# Revit family: Grab_Bar-Ligature_Resistant-Whitehall_Manufacturing_BestCare-WHB-GB_Series
name_source: partatom
category: Specialty Equipment
units: mm (PartAtom-declared; Revit-internal decimal feet)

## family parameters
Cut with Voids When Loaded = No
Host = Face
OmniClass Number = 23.40.20.21.47
OmniClass Title = Bath Grab Bars
Part Type = Normal
Room Calculation Point = No
Round Connector Dimension = Use Diameter
Shared = Yes

## types (6) — shared parameters
ADA Compliant = Yes
Assembly Code = C1030200
Bar Depth = 3 5/8"
Default Elevation = 0"
Description = Whitehall BestCare® Universal Aluminum Grab Bar
Finish = Cast Aluminum-Whitehall-Snow White (EG10) Enviro-glaze Powder Coat
Installation Instruction Link = https://www.whitehallmfg.com
Installation Type = Wall Mounted
Manufacturer = Whitehall Manufacturing
Material = Cast Aluminum-Whitehall-Snow White (EG10) Enviro-glaze Powder Coat
Product Documentation Link = https://www.whitehallmfg.com
Product Page URL = https://www.whitehallmfg.com
URL = https://www.whitehallmfg.com
Width = 4 1/2"

## per-type parameters (varying)
| type | Length | Specified Length | Type Comments |
| WHB-GB18-EG10 | 23 1/2" | 18" | 18” Universal Grab Bar |
| WHB-GB24-EG10 | 29 1/2" | 24" | 24” Universal Grab Bar |
| WHB-GB30-EG10 | 35 1/2" | 30" | 30” Universal Grab Bar |
| WHB-GB36-EG10 | 41 1/2" | 36" | 36” Universal Grab Bar |
| WHB-GB42-EG10 | 47 1/2" | 42" | 42” Universal Grab Bar |
| WHB-GB48-EG10 | 53 1/2" | 48" | 48” Universal Grab Bar |

note: column(s) folded — value = type name in every type: Model

## geometry (parser evidence)
native form markers: Sweep x3
no freeform markers — native parametric forms only
